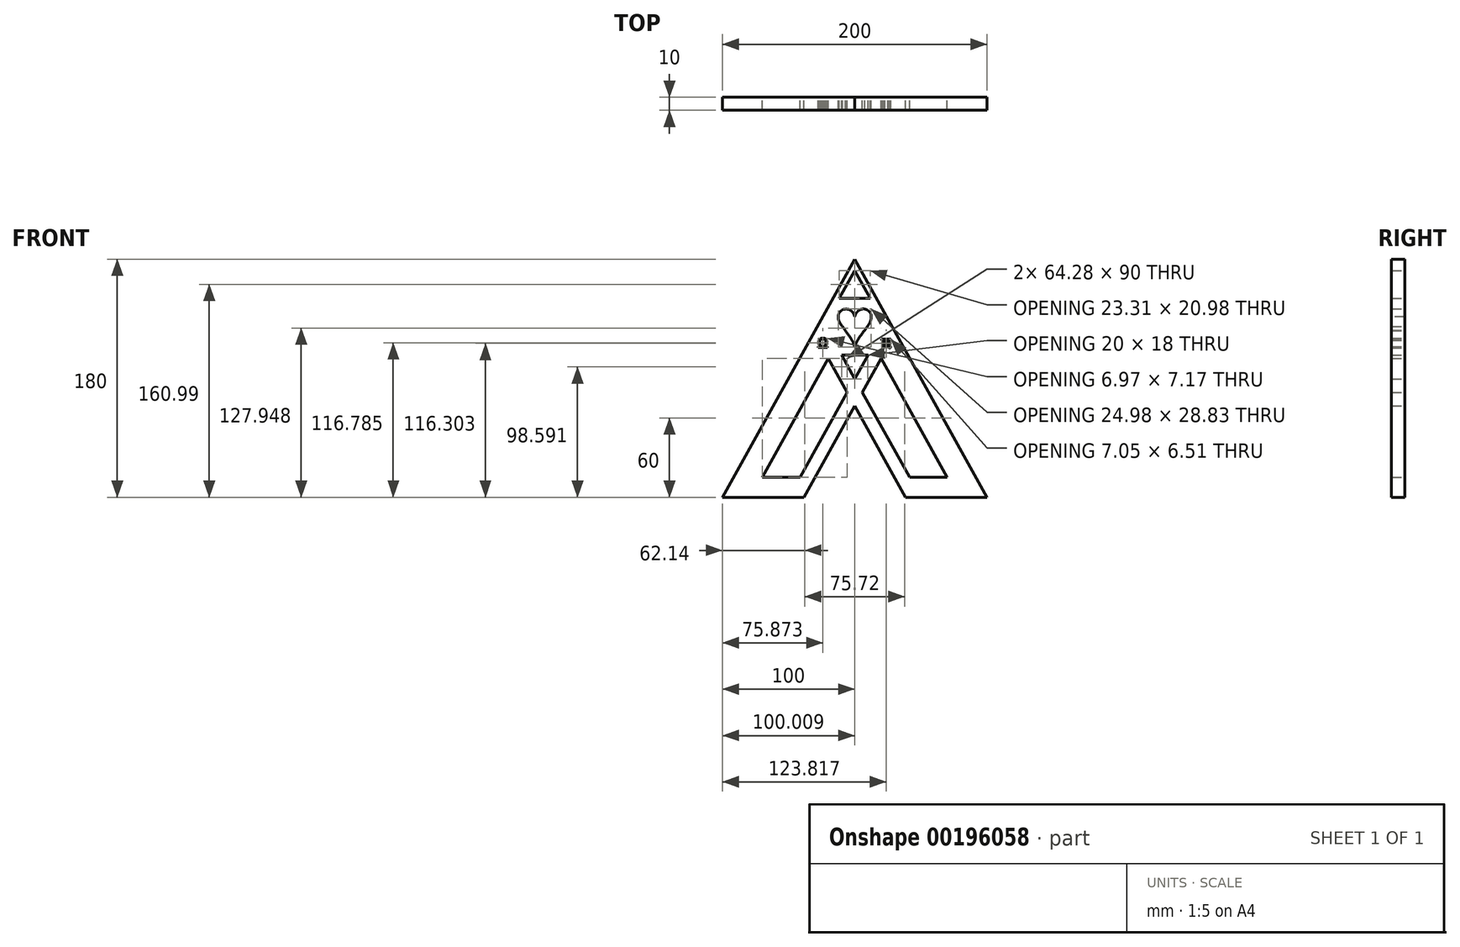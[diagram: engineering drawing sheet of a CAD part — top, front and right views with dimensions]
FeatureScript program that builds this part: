
annotation { "Feature Type Name" : "Feature", "Feature Type Description" : "" }
export const myFeature = defineFeature(function(context is Context, id is Id, definition is map)
    precondition{}
    {
        {
            var Q0;
            Q0=qCreatedBy(makeId("Front.planeOp"),FACE);
            var sketch = newSketch(context, id + "F0", { "sketchPlane" : qUnion([Q0])});
            skLineSegment(sketch, "E0", {"start": v(0, 180) * mm, "end": v(-100, 0) * mm});
            skLineSegment(sketch, "E1", {"start": v(-100, 0) * mm, "end": v(100, 0) * mm});
            skLineSegment(sketch, "E2", {"start": v(100, 0) * mm, "end": v(0, 180) * mm});
            skLineSegment(sketch, "E3", {"start": v(0, 180) * mm, "end": v(0, 0) * mm});
            skText(sketch, "E4", { "text": "♥", "fontName": "Arimo-Regular.ttf"});
            skLineSegment(sketch, "E5", {"start": v(0, 171.48) * mm, "end": v(-11.66, 150.5) * mm});
            skLineSegment(sketch, "E6", {"start": v(-11.66, 150.5) * mm, "end": v(11.66, 150.5) * mm});
            skLineSegment(sketch, "E7", {"start": v(11.66, 150.5) * mm, "end": v(0, 171.48) * mm});
            skLineSegment(sketch, "E8", {"start": v(-70, 15) * mm, "end": v(-20, 105) * mm});
            skLineSegment(sketch, "E9", {"start": v(-20, 105) * mm, "end": v(30, 15) * mm});
            skLineSegment(sketch, "E10", {"start": v(30, 15) * mm, "end": v(-70, 15) * mm});
            skLineSegment(sketch, "E11", {"start": v(-30, 15) * mm, "end": v(20, 105) * mm});
            skLineSegment(sketch, "E12", {"start": v(20, 105) * mm, "end": v(70, 15) * mm});
            skLineSegment(sketch, "E13", {"start": v(70, 15) * mm, "end": v(-30, 15) * mm});
            skLineSegment(sketch, "E14", {"start": v(-30, 15) * mm, "end": v(-38.33, 0) * mm});
            skLineSegment(sketch, "E15", {"start": v(30, 15) * mm, "end": v(38.33, 0) * mm});
            skLineSegment(sketch, "E16", {"start": v(-5.72, 79.3) * mm, "end": v(-41.44, 15) * mm});
            skLineSegment(sketch, "E17", {"start": v(5.72, 79.3) * mm, "end": v(41.44, 15) * mm});
            skLineSegment(sketch, "E18", {"start": v(0, 89.6) * mm, "end": v(-10, 107.6) * mm});
            skLineSegment(sketch, "E19", {"start": v(-10, 107.6) * mm, "end": v(10, 107.6) * mm});
            skLineSegment(sketch, "E20", {"start": v(10, 107.6) * mm, "end": v(0, 89.6) * mm});
            skText(sketch, "E21", { "text": "π", "fontName": "NotoSansCJKjp-Regular.otf"});
            skText(sketch, "E22", { "text": "Ω", "fontName": "OpenSans-Regular.ttf"});
            const initialGuessF0  = {"E4": [-0.015, 0.1141, 1, 0, 0.0364], "E21": [0.02, 0.1132, 1, 0, 0.00843], "E22": [-0.028, 0.1132, 1, 0, 0.00712]};
            skSetInitialGuess(sketch, initialGuessF0);
            skSolve(sketch);
        }
        {
            var Q0;
            {var subQ21=sQuery(id+"F0.wireOp",EDGE,"E0");Q0=makeQuery(id+"F0.imprint","IMPRINT",FACE,{"disambiguationData":[TD([[makeQuery(id+"F0.imprint","IMPRINT",EDGE,{"derivedFrom":subQ21}),1.0]])]});}
            var Q1;
            {var subQ6=sQuery(id+"F0.wireOp",EDGE,"E2");Q1=makeQuery(id+"F0.imprint","IMPRINT",FACE,{"disambiguationData":[TD([[makeQuery(id+"F0.imprint","IMPRINT",EDGE,{"derivedFrom":subQ6}),1.0]])]});}
            var Q2;
            {var subQ0=sQuery(id+"F0.wireOp",EDGE,"E16");Q2=makeQuery(id+"F0.imprint","IMPRINT",FACE,{"disambiguationData":[TD([[makeQuery(id+"F0.imprint","IMPRINT",EDGE,{"derivedFrom":subQ0}),1.0]])]});}
            var Q3;
            {var subQ5=sQuery(id+"F0.wireOp",EDGE,"E17");Q3=makeQuery(id+"F0.imprint","IMPRINT",FACE,{"disambiguationData":[TD([[makeQuery(id+"F0.imprint","IMPRINT",EDGE,{"derivedFrom":subQ5}),-1.0]])]});}
            extrude(context, id + "F1", {"entities" : qUnion([Q0, Q1, Q2, Q3]), "depth" : 10 * mm});
        }
    });
